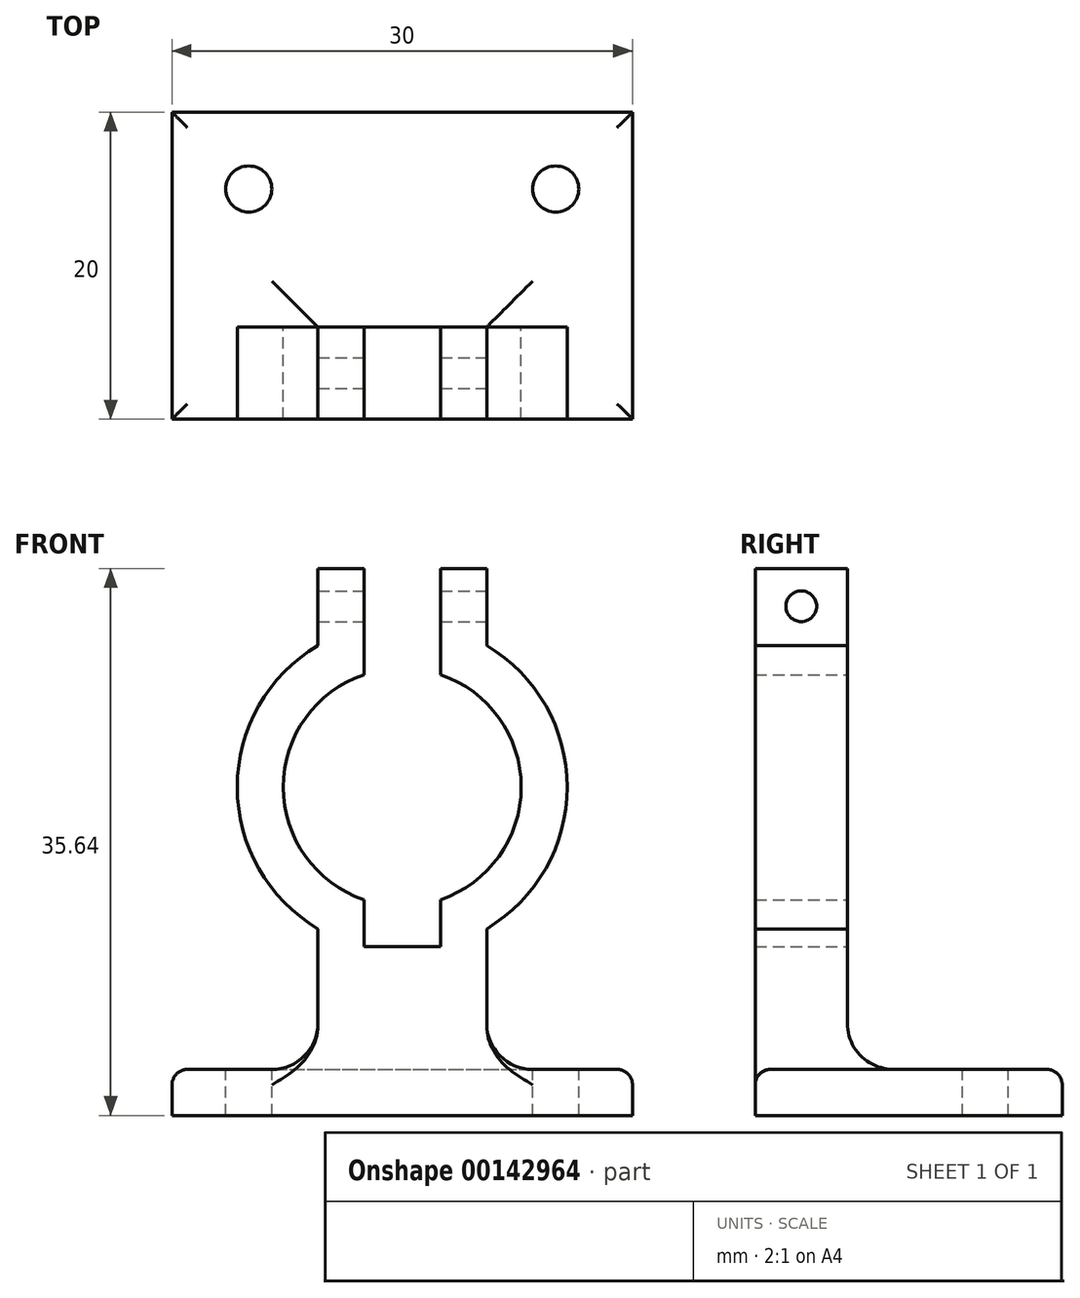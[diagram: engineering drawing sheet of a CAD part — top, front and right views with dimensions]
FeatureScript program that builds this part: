
annotation { "Feature Type Name" : "Feature", "Feature Type Description" : "" }
export const myFeature = defineFeature(function(context is Context, id is Id, definition is map)
    precondition{}
    {
        {
            var Q0;
            Q0=qCreatedBy(makeId("Front.planeOp"),FACE);
            var sketch = newSketch(context, id + "F0", { "sketchPlane" : qUnion([Q0])});
            skArc(sketch, "E0", {"start": v(-2.5, 7.34) * mm, "mid": v(-7.75, 0) * mm, "end": v(-2.5, -7.34) * mm});
            skArc(sketch, "E1", {"start": v(-5.5, 9.24) * mm, "mid": v(-10.75, 0) * mm, "end": v(-5.5, -9.24) * mm});
            skLineSegment(sketch, "E2", {"start": v(0, 0) * mm, "end": v(0, -31.22) * mm});
            skLineSegment(sketch, "E3.0", {"start": v(-2.5, 14.24) * mm, "end": v(-2.5, 7.34) * mm});
            skLineSegment(sketch, "E4.0", {"start": v(2.5, 14.24) * mm, "end": v(2.5, 7.34) * mm});
            skLineSegment(sketch, "E5", {"start": v(-20.6, 23.96) * mm, "end": v(24.86, 23.96) * mm});
            skLineSegment(sketch, "E6.0", {"start": v(5.5, 14.24) * mm, "end": v(5.5, 9.24) * mm});
            skLineSegment(sketch, "E7.0", {"start": v(-5.5, 14.24) * mm, "end": v(-5.5, 9.24) * mm});
            skLineSegment(sketch, "E8.trimOffspring", {"start": v(2.5, -7.34) * mm, "end": v(2.5, -31.22) * mm});
            skLineSegment(sketch, "E9.trimOffspring", {"start": v(-2.5, -7.34) * mm, "end": v(-2.5, -31.22) * mm});
            skLineSegment(sketch, "E10.trimOffspring", {"start": v(-5.5, -9.24) * mm, "end": v(-5.5, -31.22) * mm});
            skLineSegment(sketch, "E11.0", {"start": v(-5.5, 14.24) * mm, "end": v(-2.5, 14.24) * mm});
            skLineSegment(sketch, "E12.trimOffspring", {"start": v(2.5, 14.24) * mm, "end": v(5.5, 14.24) * mm});
            skLineSegment(sketch, "E13.0", {"start": v(-5.5, -18.46) * mm, "end": v(5.5, -18.46) * mm});
            skArc(sketch, "E14.trimOffspring", {"start": v(2.5, -7.34) * mm, "mid": v(7.75, 0) * mm, "end": v(2.5, 7.34) * mm});
            skArc(sketch, "E15.trimOffspring", {"start": v(5.5, -9.24) * mm, "mid": v(10.75, 0) * mm, "end": v(5.5, 9.24) * mm});
            skLineSegment(sketch, "E16.trimOffspring", {"start": v(5.5, -9.24) * mm, "end": v(5.5, -31.22) * mm});
            skSolve(sketch);
        }
        {
            var Q0;
            Q0 = qSketchRegion(id + "F0", true);
            extrude(context, id + "F1", {"entities" : qUnion([Q0]), "depth" : 6 * mm});
        }
        {
            var Q0;
            Q0=makeQuery(id+"F1.opExtrude","SWEPT_FACE",FACE,{"disambiguationData":[OSD([sQuery(id+"F0.wireOp",EDGE,"E6.0")])]});
            var sketch = newSketch(context, id + "F2", { "sketchPlane" : qUnion([Q0])});
            skCircle(sketch, "E17", {"center": v(-3, 11.79) * mm, "radius": 1 * mm});
            skPoint(sketch, "E17.centerSnap0", {"position": v(-3, 9.24) * mm});
            skSolve(sketch);
        }
        {
            var Q0;
            Q0=makeQuery(id+"F2.imprint","IMPRINT",FACE,{"disambiguationData":[TD([[makeQuery(id+"F2.imprint","IMPRINT",EDGE,{"derivedFrom":sQuery(id+"F2.wireOp",EDGE,"E17")}),1.0]])]});
            extrude(context, id + "F3", {"entities" : qUnion([Q0]), "operationType" : NewBodyOperationType.REMOVE, "oppositeDirection" : true, "depth" : 25 * mm});
        }
        {
            var Q0;
            Q0=qCreatedBy(makeId("Front.planeOp"),FACE);
            var sketch = newSketch(context, id + "F4", { "sketchPlane" : qUnion([Q0])});
            skLineSegment(sketch, "E18.0", {"start": v(-2.5, -7.34) * mm, "end": v(-2.5, -18.46) * mm});
            skLineSegment(sketch, "E18.1", {"start": v(2.5, -7.34) * mm, "end": v(2.5, -18.46) * mm});
            skLineSegment(sketch, "E19.bottom", {"start": v(-2.5, -12.9) * mm, "end": v(2.5, -12.9) * mm});
            skLineSegment(sketch, "E19.top", {"start": v(-2.5, -20.9) * mm, "end": v(2.5, -20.9) * mm});
            skLineSegment(sketch, "E19.left", {"start": v(-2.5, -12.9) * mm, "end": v(-2.5, -20.9) * mm});
            skLineSegment(sketch, "E19.right", {"start": v(2.5, -12.9) * mm, "end": v(2.5, -20.9) * mm});
            skLineSegment(sketch, "E20.bottom", {"start": v(15, -23.9) * mm, "end": v(-15, -23.9) * mm});
            skLineSegment(sketch, "E20.top", {"start": v(15, -20.9) * mm, "end": v(-15, -20.9) * mm});
            skLineSegment(sketch, "E20.left", {"start": v(15, -23.9) * mm, "end": v(15, -20.9) * mm});
            skLineSegment(sketch, "E20.right", {"start": v(-15, -23.9) * mm, "end": v(-15, -20.9) * mm});
            skPoint(sketch, "E20.middle", {"position": v(0, -22.4) * mm});
            skSolve(sketch);
        }
        {
            var Q0;
            {var subQ1=sQuery(id+"F4.wireOp",EDGE,"E19.bottom");Q0=makeQuery(id+"F4.imprint","IMPRINT",FACE,{"disambiguationData":[TD([[makeQuery(id+"F4.imprint","IMPRINT",EDGE,{"derivedFrom":subQ1}),-1.0]])]});}
            extrude(context, id + "F5", {"entities" : qUnion([Q0]), "depth" : 6 * mm});
        }
        {
            var Q0;
            Q0=makeQuery(id+"F4.imprint","IMPRINT",FACE,{"disambiguationData":[TD([[makeQuery(id+"F4.imprint","IMPRINT",EDGE,{"derivedFrom":sQuery(id+"F4.wireOp",EDGE,"E20.bottom")}),-1.0]])]});
            extrude(context, id + "F6", {"entities" : qUnion([Q0]), "depth" : 20 * mm, "symmetric" : true});
        }
        {
            var Q0;
            Q0=makeQuery(id+"F6.opExtrude","SWEPT_BODY",BODY,{"disambiguationData":[OSD([sQuery(id+"F4.wireOp",EDGE,"E20.bottom"),sQuery(id+"F4.wireOp",EDGE,"E20.top"),sQuery(id+"F4.wireOp",EDGE,"E20.left"),sQuery(id+"F4.wireOp",EDGE,"E20.right")])]});
            var Q1;
            Q1=makeQuery(id+"F5.opExtrude","SWEPT_BODY",BODY,{"disambiguationData":[OSD([sQuery(id+"F4.wireOp",EDGE,"E19.bottom"),sQuery(id+"F4.wireOp",EDGE,"E19.left"),sQuery(id+"F4.wireOp",EDGE,"E19.right"),sQuery(id+"F4.wireOp",EDGE,"E20.top")])]});
            transform(context, id + "F7", {"entities" : qUnion([Q0, Q1]), "transformType" : TransformType.TRANSLATION_3D, "dx" : 0 * mm, "dy" : 0 * mm, "dz" : 2.5 * mm, "makeCopy" : false});
        }
        {
            var Q0;
            Q0=makeQuery(id+"F6.opExtrude","SWEPT_BODY",BODY,{"disambiguationData":[OSD([sQuery(id+"F4.wireOp",EDGE,"E20.bottom"),sQuery(id+"F4.wireOp",EDGE,"E20.top"),sQuery(id+"F4.wireOp",EDGE,"E20.left"),sQuery(id+"F4.wireOp",EDGE,"E20.right")])]});
            transform(context, id + "F8", {"entities" : qUnion([Q0]), "transformType" : TransformType.TRANSLATION_3D, "dx" : 0 * mm, "dy" : 4 * mm, "dz" : 0 * mm, "makeCopy" : false});
        }
        {
            var Q0;
            Q0=makeQuery(id+"F5.opExtrude","SWEPT_BODY",BODY,{"disambiguationData":[OSD([sQuery(id+"F4.wireOp",EDGE,"E19.bottom"),sQuery(id+"F4.wireOp",EDGE,"E19.left"),sQuery(id+"F4.wireOp",EDGE,"E19.right"),sQuery(id+"F4.wireOp",EDGE,"E20.top")])]});
            var Q1;
            Q1=makeQuery(id+"F6.opExtrude","SWEPT_BODY",BODY,{"disambiguationData":[OSD([sQuery(id+"F4.wireOp",EDGE,"E20.bottom"),sQuery(id+"F4.wireOp",EDGE,"E20.top"),sQuery(id+"F4.wireOp",EDGE,"E20.left"),sQuery(id+"F4.wireOp",EDGE,"E20.right")])]});
            booleanBodies(context, id + "F9", {"operationType" : BooleanOperationType.UNION, "tools" : qUnion([Q0, Q1])});
        }
        {
            var Q0;
            Q0=makeQuery(id+"F5.opExtrude","SWEPT_BODY",BODY,{"disambiguationData":[OSD([sQuery(id+"F4.wireOp",EDGE,"E19.bottom"),sQuery(id+"F4.wireOp",EDGE,"E19.left"),sQuery(id+"F4.wireOp",EDGE,"E19.right"),sQuery(id+"F4.wireOp",EDGE,"E20.top")])]});
            var Q1;
            Q1=makeQuery(id+"F1.opExtrude","SWEPT_BODY",BODY,{"disambiguationData":[OSD([sQuery(id+"F0.wireOp",EDGE,"E4.0"),sQuery(id+"F0.wireOp",EDGE,"E6.0"),sQuery(id+"F0.wireOp",EDGE,"E8.trimOffspring"),sQuery(id+"F0.wireOp",EDGE,"E12.trimOffspring"),sQuery(id+"F0.wireOp",EDGE,"E13.0"),sQuery(id+"F0.wireOp",EDGE,"E14.trimOffspring"),sQuery(id+"F0.wireOp",EDGE,"E15.trimOffspring"),sQuery(id+"F0.wireOp",EDGE,"E16.trimOffspring")])]});
            var Q2;
            Q2=makeQuery(id+"F1.opExtrude","SWEPT_BODY",BODY,{"disambiguationData":[OSD([sQuery(id+"F0.wireOp",EDGE,"E0"),sQuery(id+"F0.wireOp",EDGE,"E1"),sQuery(id+"F0.wireOp",EDGE,"E3.0"),sQuery(id+"F0.wireOp",EDGE,"E7.0"),sQuery(id+"F0.wireOp",EDGE,"E9.trimOffspring"),sQuery(id+"F0.wireOp",EDGE,"E10.trimOffspring"),sQuery(id+"F0.wireOp",EDGE,"E11.0"),sQuery(id+"F0.wireOp",EDGE,"E13.0")])]});
            booleanBodies(context, id + "F10", {"operationType" : BooleanOperationType.UNION, "tools" : qUnion([Q0, Q1, Q2])});
        }
        {
            var Q0;
            {var subQ0=sQuery(id+"F4.wireOp",EDGE,"E20.top");var subQ2=sQuery(id+"F4.wireOp",EDGE,"E19.left");Q0=makeQuery(id+"F9.opBoolean","SPLIT",EDGE,{"disambiguationData":[TD([makeQuery(id+"F5.opExtrude","SWEPT_FACE",FACE,{"disambiguationData":[OSD([subQ2])]})])],"derivedFrom":makeQuery(id+"F6.opExtrude","CAP_EDGE",EDGE,{"disambiguationData":[OSD([subQ0])],"isStart":false})});}
            var Q1;
            {var subQ1=sQuery(id+"F4.wireOp",EDGE,"E20.top");var subQ2=sQuery(id+"F4.wireOp",EDGE,"E19.right");Q1=makeQuery(id+"F9.opBoolean","SPLIT",EDGE,{"disambiguationData":[TD([makeQuery(id+"F5.opExtrude","SWEPT_FACE",FACE,{"disambiguationData":[OSD([subQ2])]})])],"derivedFrom":makeQuery(id+"F6.opExtrude","CAP_EDGE",EDGE,{"disambiguationData":[OSD([subQ1])],"isStart":false})});}
            var Q2;
            Q2=makeQuery(id+"F6.opExtrude","SWEPT_EDGE",EDGE,{"disambiguationData":[OSD([sQuery(id+"F4.wireOp",EDGE,"E20.top"),sQuery(id+"F4.wireOp",EDGE,"E20.left")])]});
            var Q3;
            Q3=makeQuery(id+"F6.opExtrude","CAP_EDGE",EDGE,{"disambiguationData":[OSD([sQuery(id+"F4.wireOp",EDGE,"E20.top")])],"isStart":true});
            var Q4;
            Q4=makeQuery(id+"F6.opExtrude","SWEPT_EDGE",EDGE,{"disambiguationData":[OSD([sQuery(id+"F4.wireOp",EDGE,"E20.top"),sQuery(id+"F4.wireOp",EDGE,"E20.right")])]});
            fillet(context, id + "F11", {"entities" : qUnion([Q0, Q1, Q2, Q3, Q4]), "radius" : 1 * mm, "tangentPropagation" : true, "allowEdgeOverflow" : false});
        }
        {
            var Q0;
            Q0=makeQuery(id+"F10.opBoolean","INTERSECT",EDGE,{"derivedFrom":[makeQuery(id+"F1.opExtrude","SWEPT_FACE",FACE,{"disambiguationData":[OSD([sQuery(id+"F0.wireOp",EDGE,"E10.trimOffspring")])]}),makeQuery(id+"F6.opExtrude","SWEPT_FACE",FACE,{"disambiguationData":[OSD([sQuery(id+"F4.wireOp",EDGE,"E20.top")])]})]});
            var Q1;
            {var subQ0=sQuery(id+"F0.wireOp",EDGE,"E13.0");Q1=makeQuery(id+"F10.opBoolean","INTERSECT",EDGE,{"derivedFrom":[makeQuery(id+"F1.opExtrude","CAP_FACE",FACE,{"disambiguationData":[OSD([sQuery(id+"F0.wireOp",EDGE,"E0"),sQuery(id+"F0.wireOp",EDGE,"E1"),sQuery(id+"F0.wireOp",EDGE,"E3.0"),sQuery(id+"F0.wireOp",EDGE,"E7.0"),sQuery(id+"F0.wireOp",EDGE,"E9.trimOffspring"),sQuery(id+"F0.wireOp",EDGE,"E10.trimOffspring"),sQuery(id+"F0.wireOp",EDGE,"E11.0"),subQ0])],"isStart":true}),makeQuery(id+"F1.opExtrude","CAP_FACE",FACE,{"disambiguationData":[OSD([sQuery(id+"F0.wireOp",EDGE,"E4.0"),sQuery(id+"F0.wireOp",EDGE,"E6.0"),sQuery(id+"F0.wireOp",EDGE,"E8.trimOffspring"),sQuery(id+"F0.wireOp",EDGE,"E12.trimOffspring"),subQ0,sQuery(id+"F0.wireOp",EDGE,"E14.trimOffspring"),sQuery(id+"F0.wireOp",EDGE,"E15.trimOffspring"),sQuery(id+"F0.wireOp",EDGE,"E16.trimOffspring")])],"isStart":true}),makeQuery(id+"F6.opExtrude","SWEPT_FACE",FACE,{"disambiguationData":[OSD([sQuery(id+"F4.wireOp",EDGE,"E20.top")])]})]});}
            var Q2;
            Q2=makeQuery(id+"F10.opBoolean","INTERSECT",EDGE,{"derivedFrom":[makeQuery(id+"F1.opExtrude","SWEPT_FACE",FACE,{"disambiguationData":[OSD([sQuery(id+"F0.wireOp",EDGE,"E16.trimOffspring")])]}),makeQuery(id+"F6.opExtrude","SWEPT_FACE",FACE,{"disambiguationData":[OSD([sQuery(id+"F4.wireOp",EDGE,"E20.top")])]})]});
            fillet(context, id + "F12", {"entities" : qUnion([Q0, Q1, Q2]), "radius" : 3 * mm, "tangentPropagation" : true, "allowEdgeOverflow" : false});
        }
        {
            var Q0;
            Q0=makeQuery(id+"F6.opExtrude","SWEPT_FACE",FACE,{"disambiguationData":[OSD([sQuery(id+"F4.wireOp",EDGE,"E20.top")])]});
            var sketch = newSketch(context, id + "F13", { "sketchPlane" : qUnion([Q0])});
            skCircle(sketch, "E21", {"center": v(-10, 9) * mm, "radius": 1.5 * mm});
            skCircle(sketch, "E22", {"center": v(10, 9) * mm, "radius": 1.5 * mm});
            skSolve(sketch);
        }
        {
            var Q0;
            Q0 = qSketchRegion(id + "F13", true);
            extrude(context, id + "F14", {"entities" : qUnion([Q0]), "operationType" : NewBodyOperationType.REMOVE, "oppositeDirection" : true, "depth" : 25 * mm});
        }
    });
